# Revit family: PROOX Paper towel dispenser EN
name_source: partatom
category: Furniture
revit_build: Autodesk Revit 2014 (Build: 20130308_1515(x64)
units: mm (PartAtom-declared; Revit-internal decimal feet)

## types (2) — shared parameters
BIM objects producer = www.BIMtelligent.eu
Manufacturer = PROOX Ltd.
Product data sheet = http://www.proox.com
URL = http://www.proox.com
zero-valued in all types: Default Elevation

## per-type parameters (varying)
| type | Cost | Description | EAN-No. | Material | Model | Specification |
| ONE dark passion | 245 $ | handdryer PROOX ONE dark passion made from aluminum black anodized | 9120050350168 | Aluminum, black anodised | DP-100 | Powerful hand dryer made out from glass pearl blasted and black anodised aluminum. Cover 3 mm thickness. Intended for wall mounting, with optoelectronic sensor. Perforated design area with 4mm drillings. Drying time less then 10 seconds. Air temperature 55°C, 500W motor, 500W heater element, Air output adjustable as well as the sensor detection range from 5 to 33cm. Automatic switch-off mode after 60 sec. Includes stainless steel screws and anchors. Cables for installation not included. |
| ONE pure | 215 $ | paper towel dispenser PROOX ONE pure made from stainless steel | 9120050350021 | Stainless steel, brushed | PU-100 | Paper towel dispenser made out of stainless steel. Surface with fine brushed structure. Cover 1.5 mm thickness. Intended for wall mounting. Perforated fill level indicator with 4mm drillings. Integrated Teflon-coated soft-slide box for easy paper dispensing. Holds 300-400 accordion-fold paper towels. Lock not visible. Includes stainless steel screws and anchors. |

note: column(s) folded — value = type name in every type: Type Comments

## geometry (parser evidence)
native form markers: Sweep x1
no freeform markers — native parametric forms only
